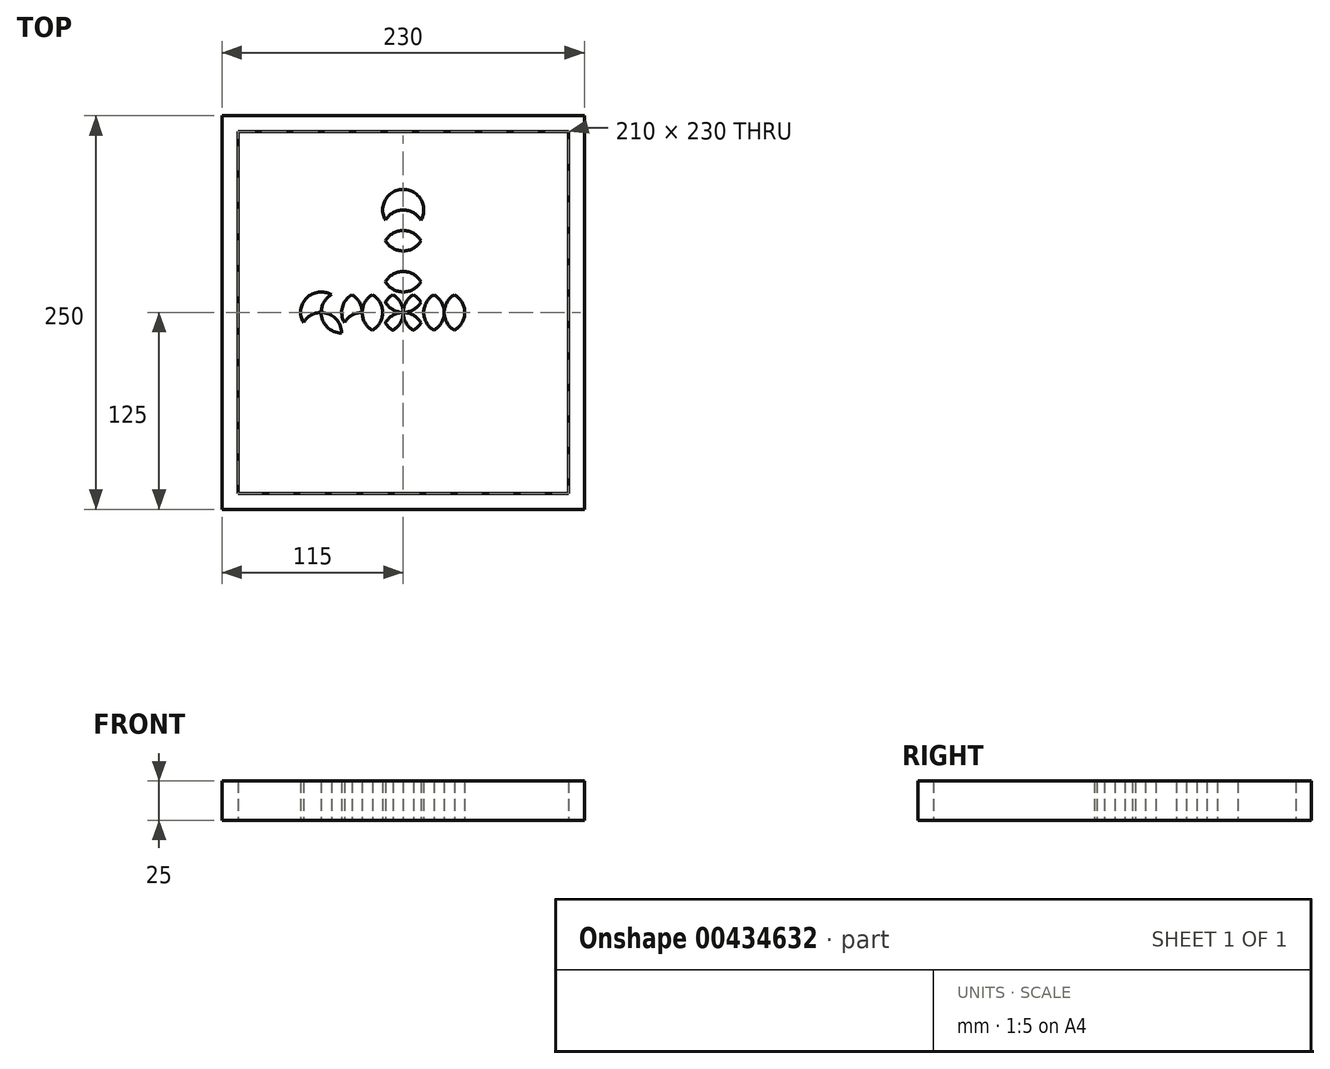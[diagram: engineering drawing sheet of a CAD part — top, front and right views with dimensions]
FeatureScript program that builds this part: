
annotation { "Feature Type Name" : "Feature", "Feature Type Description" : "" }
export const myFeature = defineFeature(function(context is Context, id is Id, definition is map)
    precondition{}
    {
        {
            var Q0;
            Q0=qCreatedBy(makeId("Top.planeOp"),FACE);
            var sketch = newSketch(context, id + "F0", { "sketchPlane" : qUnion([Q0])});
            skLineSegment(sketch, "E0.bottom", {"start": v(-115, -125) * mm, "end": v(115, -125) * mm});
            skLineSegment(sketch, "E0.top", {"start": v(-115, 125) * mm, "end": v(115, 125) * mm});
            skLineSegment(sketch, "E0.left", {"start": v(-115, -125) * mm, "end": v(-115, 125) * mm});
            skLineSegment(sketch, "E0.right", {"start": v(115, -125) * mm, "end": v(115, 125) * mm});
            skPoint(sketch, "E0.middle", {"position": v(0, 0) * mm});
            skLineSegment(sketch, "E1.0", {"start": v(-105, -115) * mm, "end": v(-105, 115) * mm});
            skLineSegment(sketch, "E1.1", {"start": v(-105, -115) * mm, "end": v(105, -115) * mm});
            skLineSegment(sketch, "E1.2", {"start": v(105, -115) * mm, "end": v(105, 115) * mm});
            skLineSegment(sketch, "E1.3", {"start": v(-105, 115) * mm, "end": v(105, 115) * mm});
            skSolve(sketch);
        }
        {
            var Q0;
            Q0=makeQuery(id+"F0.imprint","IMPRINT",FACE,{"disambiguationData":[TD([[makeQuery(id+"F0.imprint","IMPRINT",EDGE,{"derivedFrom":sQuery(id+"F0.wireOp",EDGE,"E0.bottom")}),1.0]])]});
            extrude(context, id + "F1", {"entities" : qUnion([Q0]), "depth" : 25 * mm});
        }
        {
            var Q0;
            Q0=qCreatedBy(makeId("Top.planeOp"),FACE);
            var sketch = newSketch(context, id + "F2", { "sketchPlane" : qUnion([Q0])});
            skCircle(sketch, "E2", {"center": v(0, 0) * mm, "radius": 13.03 * mm});
            skCircle(sketch, "E3", {"center": v(-13.03, 0) * mm, "radius": 13.03 * mm});
            skCircle(sketch, "E4", {"center": v(13.03, 0) * mm, "radius": 13.03 * mm});
            skCircle(sketch, "E5", {"center": v(-26.05, 0) * mm, "radius": 13.03 * mm});
            skCircle(sketch, "E6", {"center": v(-39.08, 0) * mm, "radius": 13.03 * mm});
            skCircle(sketch, "E7", {"center": v(-52.1, 0) * mm, "radius": 13.03 * mm});
            skCircle(sketch, "E8", {"center": v(26.05, 0) * mm, "radius": 13.03 * mm});
            skCircle(sketch, "E9", {"center": v(39.08, 0) * mm, "radius": 13.03 * mm});
            skCircle(sketch, "E10", {"center": v(0, 13.03) * mm, "radius": 13.03 * mm});
            skCircle(sketch, "E11", {"center": v(0, 26.05) * mm, "radius": 13.03 * mm});
            skCircle(sketch, "E12", {"center": v(0, 39.08) * mm, "radius": 13.03 * mm});
            skCircle(sketch, "E13", {"center": v(0, 52.1) * mm, "radius": 13.03 * mm});
            skCircle(sketch, "E14", {"center": v(0, 65.13) * mm, "radius": 13.03 * mm});
            skCircle(sketch, "E15", {"center": v(-26.05, -13.03) * mm, "radius": 13.03 * mm});
            skCircle(sketch, "E16", {"center": v(-52.1, -13.03) * mm, "radius": 13.03 * mm});
            skCircle(sketch, "E17", {"center": v(0, -13.03) * mm, "radius": 13.03 * mm});
            skCircle(sketch, "E18", {"center": v(26.05, -13.03) * mm, "radius": 13.03 * mm});
            skSolve(sketch);
        }
        {
            var Q0;
            {var subQ0=sQuery(id+"F2.wireOp",EDGE,"E14");var subQ1=sQuery(id+"F2.wireOp",EDGE,"E13");var subQ2=makeQuery(id+"F2.imprint","INTERSECT",VERTEX,{"disambiguationData":[OD(0.0)],"derivedFrom":[subQ1,subQ0]});Q0=makeQuery(id+"F2.imprint","IMPRINT",FACE,{"disambiguationData":[TD([[makeQuery(id+"F2.imprint","IMPRINT",EDGE,{"disambiguationData":[TD([[subQ2,1.0]])],"derivedFrom":subQ1}),-1.0]])]});}
            var Q1;
            {var subQ0=sQuery(id+"F2.wireOp",EDGE,"E13");var subQ1=sQuery(id+"F2.wireOp",EDGE,"E12");var subQ2=makeQuery(id+"F2.imprint","INTERSECT",VERTEX,{"disambiguationData":[OD(0.0)],"derivedFrom":[subQ1,subQ0]});Q1=makeQuery(id+"F2.imprint","IMPRINT",FACE,{"disambiguationData":[TD([[makeQuery(id+"F2.imprint","IMPRINT",EDGE,{"disambiguationData":[TD([[subQ2,-1.0]])],"derivedFrom":subQ1}),1.0]])]});}
            var Q2;
            {var subQ0=sQuery(id+"F2.wireOp",EDGE,"E11");var subQ1=sQuery(id+"F2.wireOp",EDGE,"E10");var subQ2=makeQuery(id+"F2.imprint","INTERSECT",VERTEX,{"disambiguationData":[OD(0.0)],"derivedFrom":[subQ1,subQ0]});Q2=makeQuery(id+"F2.imprint","IMPRINT",FACE,{"disambiguationData":[TD([[makeQuery(id+"F2.imprint","IMPRINT",EDGE,{"disambiguationData":[TD([[subQ2,-1.0]])],"derivedFrom":subQ1}),1.0]])]});}
            var Q3;
            {var subQ0=sQuery(id+"F2.wireOp",EDGE,"E10");var subQ1=sQuery(id+"F2.wireOp",EDGE,"E2");var subQ2=makeQuery(id+"F2.imprint","INTERSECT",VERTEX,{"disambiguationData":[OD(0.0)],"derivedFrom":[subQ1,subQ0]});Q3=makeQuery(id+"F2.imprint","IMPRINT",FACE,{"disambiguationData":[TD([[makeQuery(id+"F2.imprint","IMPRINT",EDGE,{"disambiguationData":[TD([[subQ2,-1.0]])],"derivedFrom":subQ1}),1.0]])]});}
            var Q4;
            {var subQ0=sQuery(id+"F2.wireOp",EDGE,"E3");var subQ1=sQuery(id+"F2.wireOp",EDGE,"E2");var subQ2=makeQuery(id+"F2.imprint","INTERSECT",VERTEX,{"disambiguationData":[OD(0.0)],"derivedFrom":[subQ1,subQ0]});Q4=makeQuery(id+"F2.imprint","IMPRINT",FACE,{"disambiguationData":[TD([[makeQuery(id+"F2.imprint","IMPRINT",EDGE,{"disambiguationData":[TD([[subQ2,-1.0]])],"derivedFrom":subQ1}),1.0]])]});}
            var Q5;
            {var subQ0=sQuery(id+"F2.wireOp",EDGE,"E17");var subQ1=sQuery(id+"F2.wireOp",EDGE,"E2");var subQ2=makeQuery(id+"F2.imprint","INTERSECT",VERTEX,{"disambiguationData":[OD(0.0)],"derivedFrom":[subQ1,subQ0]});Q5=makeQuery(id+"F2.imprint","IMPRINT",FACE,{"disambiguationData":[TD([[makeQuery(id+"F2.imprint","IMPRINT",EDGE,{"disambiguationData":[TD([[subQ2,-1.0]])],"derivedFrom":subQ1}),1.0]])]});}
            var Q6;
            {var subQ0=sQuery(id+"F2.wireOp",EDGE,"E4");var subQ1=sQuery(id+"F2.wireOp",EDGE,"E2");var subQ2=makeQuery(id+"F2.imprint","INTERSECT",VERTEX,{"disambiguationData":[OD(1.0)],"derivedFrom":[subQ1,subQ0]});Q6=makeQuery(id+"F2.imprint","IMPRINT",FACE,{"disambiguationData":[TD([[makeQuery(id+"F2.imprint","IMPRINT",EDGE,{"disambiguationData":[TD([[subQ2,-1.0]])],"derivedFrom":subQ1}),1.0]])]});}
            var Q7;
            {var subQ0=sQuery(id+"F2.wireOp",EDGE,"E6");var subQ1=sQuery(id+"F2.wireOp",EDGE,"E5");var subQ2=makeQuery(id+"F2.imprint","INTERSECT",VERTEX,{"disambiguationData":[OD(0.0)],"derivedFrom":[subQ1,subQ0]});Q7=makeQuery(id+"F2.imprint","IMPRINT",FACE,{"disambiguationData":[TD([[makeQuery(id+"F2.imprint","IMPRINT",EDGE,{"disambiguationData":[TD([[subQ2,-1.0]])],"derivedFrom":subQ1}),1.0]])]});}
            var Q8;
            {var subQ0=sQuery(id+"F2.wireOp",EDGE,"E5");var subQ1=sQuery(id+"F2.wireOp",EDGE,"E3");var subQ2=makeQuery(id+"F2.imprint","INTERSECT",VERTEX,{"disambiguationData":[OD(1.0)],"derivedFrom":[subQ1,subQ0]});Q8=makeQuery(id+"F2.imprint","IMPRINT",FACE,{"disambiguationData":[TD([[makeQuery(id+"F2.imprint","IMPRINT",EDGE,{"disambiguationData":[TD([[subQ2,-1.0]])],"derivedFrom":subQ0}),1.0]])]});}
            var Q9;
            {var subQ0=sQuery(id+"F2.wireOp",EDGE,"E5");var subQ1=sQuery(id+"F2.wireOp",EDGE,"E3");var subQ2=makeQuery(id+"F2.imprint","INTERSECT",VERTEX,{"disambiguationData":[OD(0.0)],"derivedFrom":[subQ1,subQ0]});Q9=makeQuery(id+"F2.imprint","IMPRINT",FACE,{"disambiguationData":[TD([[makeQuery(id+"F2.imprint","IMPRINT",EDGE,{"disambiguationData":[TD([[subQ2,1.0]])],"derivedFrom":subQ0}),1.0]])]});}
            var Q10;
            {var subQ0=sQuery(id+"F2.wireOp",EDGE,"E16");var subQ1=sQuery(id+"F2.wireOp",EDGE,"E6");var subQ2=makeQuery(id+"F2.imprint","INTERSECT",VERTEX,{"derivedFrom":[subQ1,subQ0]});Q10=makeQuery(id+"F2.imprint","IMPRINT",FACE,{"disambiguationData":[TD([[makeQuery(id+"F2.imprint","IMPRINT",EDGE,{"disambiguationData":[TD([[subQ2,-1.0]])],"derivedFrom":subQ1}),1.0]])]});}
            var Q11;
            {var subQ0=sQuery(id+"F2.wireOp",EDGE,"E7");var subQ1=sQuery(id+"F2.wireOp",EDGE,"E6");var subQ2=makeQuery(id+"F2.imprint","INTERSECT",VERTEX,{"disambiguationData":[OD(1.0)],"derivedFrom":[subQ1,subQ0]});Q11=makeQuery(id+"F2.imprint","IMPRINT",FACE,{"disambiguationData":[TD([[makeQuery(id+"F2.imprint","IMPRINT",EDGE,{"disambiguationData":[TD([[subQ2,-1.0]])],"derivedFrom":subQ0}),-1.0]])]});}
            var Q12;
            {var subQ0=sQuery(id+"F2.wireOp",EDGE,"E7");var subQ1=sQuery(id+"F2.wireOp",EDGE,"E6");var subQ2=makeQuery(id+"F2.imprint","INTERSECT",VERTEX,{"disambiguationData":[OD(0.0)],"derivedFrom":[subQ1,subQ0]});Q12=makeQuery(id+"F2.imprint","IMPRINT",FACE,{"disambiguationData":[TD([[makeQuery(id+"F2.imprint","IMPRINT",EDGE,{"disambiguationData":[TD([[subQ2,-1.0]])],"derivedFrom":subQ1}),-1.0]])]});}
            var Q13;
            {var subQ0=sQuery(id+"F2.wireOp",EDGE,"E8");var subQ1=sQuery(id+"F2.wireOp",EDGE,"E4");var subQ2=makeQuery(id+"F2.imprint","INTERSECT",VERTEX,{"disambiguationData":[OD(1.0)],"derivedFrom":[subQ1,subQ0]});Q13=makeQuery(id+"F2.imprint","IMPRINT",FACE,{"disambiguationData":[TD([[makeQuery(id+"F2.imprint","IMPRINT",EDGE,{"disambiguationData":[TD([[subQ2,1.0]])],"derivedFrom":subQ0}),1.0]])]});}
            var Q14;
            {var subQ0=sQuery(id+"F2.wireOp",EDGE,"E8");var subQ1=sQuery(id+"F2.wireOp",EDGE,"E4");var subQ2=makeQuery(id+"F2.imprint","INTERSECT",VERTEX,{"disambiguationData":[OD(0.0)],"derivedFrom":[subQ1,subQ0]});Q14=makeQuery(id+"F2.imprint","IMPRINT",FACE,{"disambiguationData":[TD([[makeQuery(id+"F2.imprint","IMPRINT",EDGE,{"disambiguationData":[TD([[subQ2,-1.0]])],"derivedFrom":subQ0}),1.0]])]});}
            var Q15;
            {var subQ0=sQuery(id+"F2.wireOp",EDGE,"E9");var subQ1=sQuery(id+"F2.wireOp",EDGE,"E8");var subQ2=makeQuery(id+"F2.imprint","INTERSECT",VERTEX,{"disambiguationData":[OD(1.0)],"derivedFrom":[subQ1,subQ0]});Q15=makeQuery(id+"F2.imprint","IMPRINT",FACE,{"disambiguationData":[TD([[makeQuery(id+"F2.imprint","IMPRINT",EDGE,{"disambiguationData":[TD([[subQ2,-1.0]])],"derivedFrom":subQ1}),1.0]])]});}
            var Q16;
            {var subQ0=sQuery(id+"F2.wireOp",EDGE,"E9");var subQ1=sQuery(id+"F2.wireOp",EDGE,"E8");var subQ2=makeQuery(id+"F2.imprint","INTERSECT",VERTEX,{"disambiguationData":[OD(0.0)],"derivedFrom":[subQ1,subQ0]});Q16=makeQuery(id+"F2.imprint","IMPRINT",FACE,{"disambiguationData":[TD([[makeQuery(id+"F2.imprint","IMPRINT",EDGE,{"disambiguationData":[TD([[subQ2,1.0]])],"derivedFrom":subQ1}),1.0]])]});}
            extrude(context, id + "F3", {"entities" : qUnion([Q0, Q1, Q2, Q3, Q4, Q5, Q6, Q7, Q8, Q9, Q10, Q11, Q12, Q13, Q14, Q15, Q16]), "depth" : 25 * mm});
        }
    });
